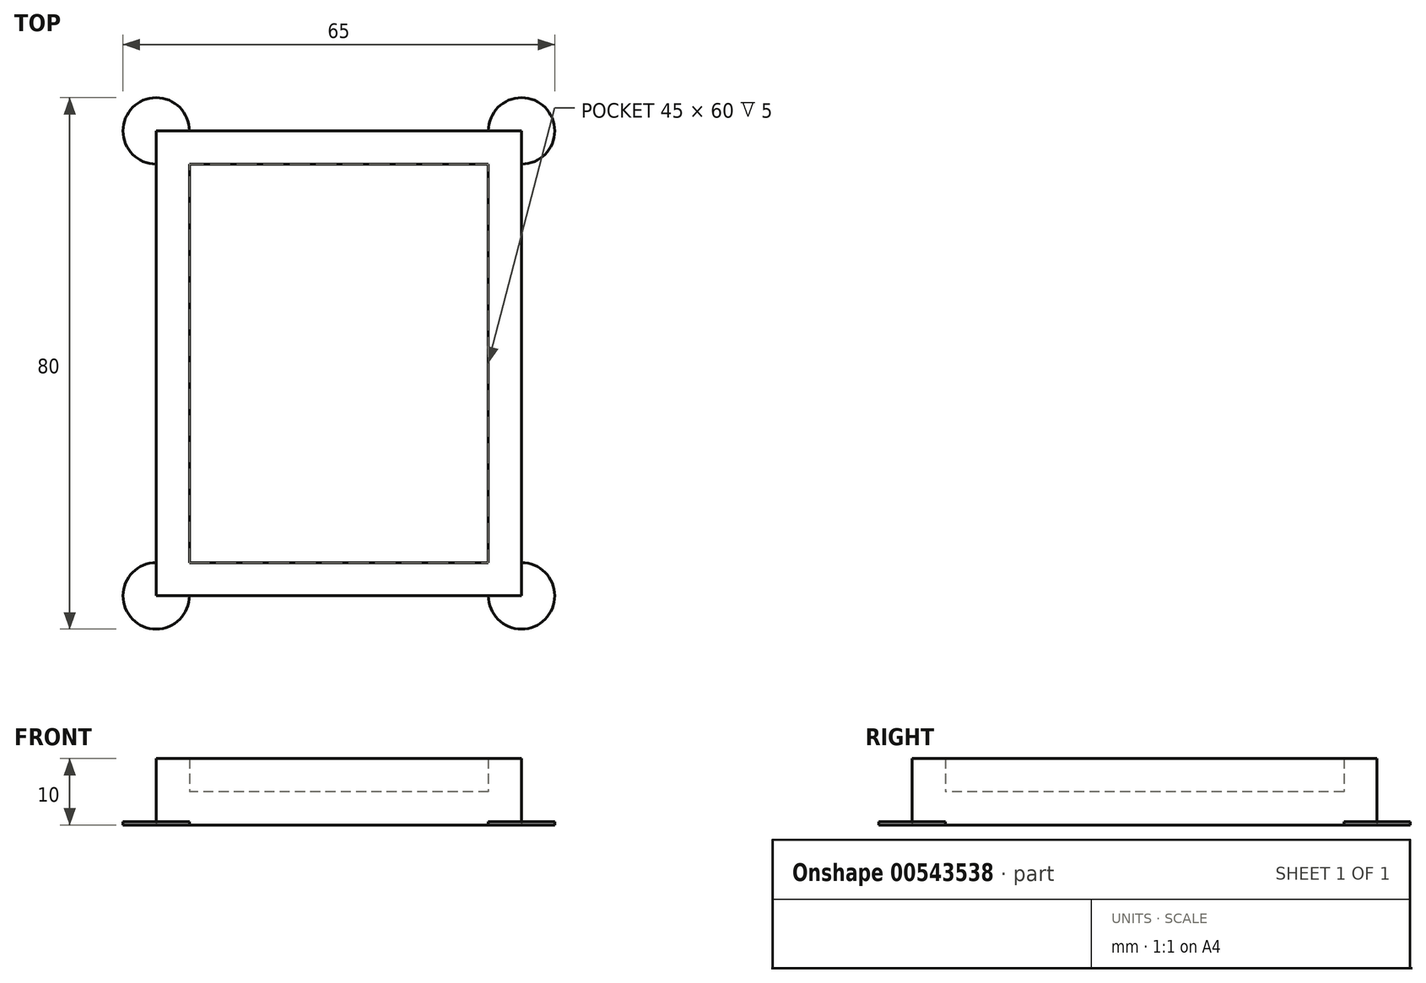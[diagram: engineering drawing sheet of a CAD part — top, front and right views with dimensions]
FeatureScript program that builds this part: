
annotation { "Feature Type Name" : "Feature", "Feature Type Description" : "" }
export const myFeature = defineFeature(function(context is Context, id is Id, definition is map)
    precondition{}
    {
        {
            var Q0;
            Q0=qCreatedBy(makeId("Top.planeOp"),FACE);
            var sketch = newSketch(context, id + "F0", { "sketchPlane" : qUnion([Q0])});
            skLineSegment(sketch, "E0.bottom", {"start": v(1016, -881.74) * mm, "end": v(-1016, -881.74) * mm});
            skLineSegment(sketch, "E0.top", {"start": v(1016, 881.74) * mm, "end": v(-1016, 881.74) * mm});
            skLineSegment(sketch, "E0.left", {"start": v(1016, -881.74) * mm, "end": v(1016, 881.74) * mm});
            skLineSegment(sketch, "E0.right", {"start": v(-1016, -881.74) * mm, "end": v(-1016, 881.74) * mm});
            skPoint(sketch, "E0.middle", {"position": v(0, 0) * mm});
            skLineSegment(sketch, "E1.bottom", {"start": v(22.5, 30) * mm, "end": v(-22.5, 30) * mm});
            skLineSegment(sketch, "E1.top", {"start": v(22.5, -30) * mm, "end": v(-22.5, -30) * mm});
            skLineSegment(sketch, "E1.left", {"start": v(22.5, 30) * mm, "end": v(22.5, -30) * mm});
            skLineSegment(sketch, "E1.right", {"start": v(-22.5, 30) * mm, "end": v(-22.5, -30) * mm});
            skLineSegment(sketch, "E2.0", {"start": v(27.5, 35) * mm, "end": v(27.5, -35) * mm});
            skLineSegment(sketch, "E2.1", {"start": v(27.5, 35) * mm, "end": v(-27.5, 35) * mm});
            skLineSegment(sketch, "E2.2", {"start": v(-27.5, 35) * mm, "end": v(-27.5, -35) * mm});
            skLineSegment(sketch, "E2.3", {"start": v(27.5, -35) * mm, "end": v(-27.5, -35) * mm});
            skSolve(sketch);
        }
        {
            var Q0;
            Q0=makeQuery(id+"F0.imprint","IMPRINT",FACE,{"disambiguationData":[TD([[makeQuery(id+"F0.imprint","IMPRINT",EDGE,{"derivedFrom":sQuery(id+"F0.wireOp",EDGE,"E1.bottom")}),-1.0]])]});
            extrude(context, id + "F1", {"entities" : qUnion([Q0]), "depth" : 5 * mm, "offsetDistance" : 25 * mm});
        }
        {
            var Q0;
            Q0=makeQuery(id+"F1.opExtrude","CAP_FACE",FACE,{"disambiguationData":[OSD([sQuery(id+"F0.wireOp",EDGE,"E1.bottom"),sQuery(id+"F0.wireOp",EDGE,"E1.top"),sQuery(id+"F0.wireOp",EDGE,"E1.left"),sQuery(id+"F0.wireOp",EDGE,"E1.right"),sQuery(id+"F0.wireOp",EDGE,"E2.0"),sQuery(id+"F0.wireOp",EDGE,"E2.1"),sQuery(id+"F0.wireOp",EDGE,"E2.2"),sQuery(id+"F0.wireOp",EDGE,"E2.3")])],"isStart":true});
            var sketch = newSketch(context, id + "F2", { "sketchPlane" : qUnion([Q0])});
            skLineSegment(sketch, "E3.bottom", {"start": v(27.5, 35) * mm, "end": v(-27.5, 35) * mm});
            skLineSegment(sketch, "E3.top", {"start": v(27.5, -35) * mm, "end": v(-27.5, -35) * mm});
            skLineSegment(sketch, "E3.left", {"start": v(27.5, 35) * mm, "end": v(27.5, -35) * mm});
            skLineSegment(sketch, "E3.right", {"start": v(-27.5, 35) * mm, "end": v(-27.5, -35) * mm});
            skPoint(sketch, "E3.middle", {"position": v(0, 0) * mm});
            skSolve(sketch);
        }
        {
            var Q0;
            Q0 = qSketchRegion(id + "F2", true);
            extrude(context, id + "F3", {"entities" : qUnion([Q0]), "operationType" : NewBodyOperationType.ADD, "depth" : 5 * mm, "offsetDistance" : 25 * mm});
        }
        {
            var Q0;
            Q0=makeQuery(id+"F3.opExtrude","CAP_FACE",FACE,{"disambiguationData":[OSD([sQuery(id+"F2.wireOp",EDGE,"E3.bottom"),sQuery(id+"F2.wireOp",EDGE,"E3.top"),sQuery(id+"F2.wireOp",EDGE,"E3.left"),sQuery(id+"F2.wireOp",EDGE,"E3.right")])],"isStart":false});
            var sketch = newSketch(context, id + "F4", { "sketchPlane" : qUnion([Q0])});
            skCircle(sketch, "E4", {"center": v(-27.5, 35) * mm, "radius": 5 * mm});
            skCircle(sketch, "E5", {"center": v(27.5, 35) * mm, "radius": 5 * mm});
            skCircle(sketch, "E6", {"center": v(27.5, -35) * mm, "radius": 5 * mm});
            skCircle(sketch, "E7", {"center": v(-27.5, -35) * mm, "radius": 5 * mm});
            skSolve(sketch);
        }
        {
            var Q0;
            Q0 = qSketchRegion(id + "F4", true);
            extrude(context, id + "F5", {"entities" : qUnion([Q0]), "operationType" : NewBodyOperationType.ADD, "oppositeDirection" : true, "depth" : 0.5 * mm, "offsetDistance" : 25 * mm});
        }
    });
